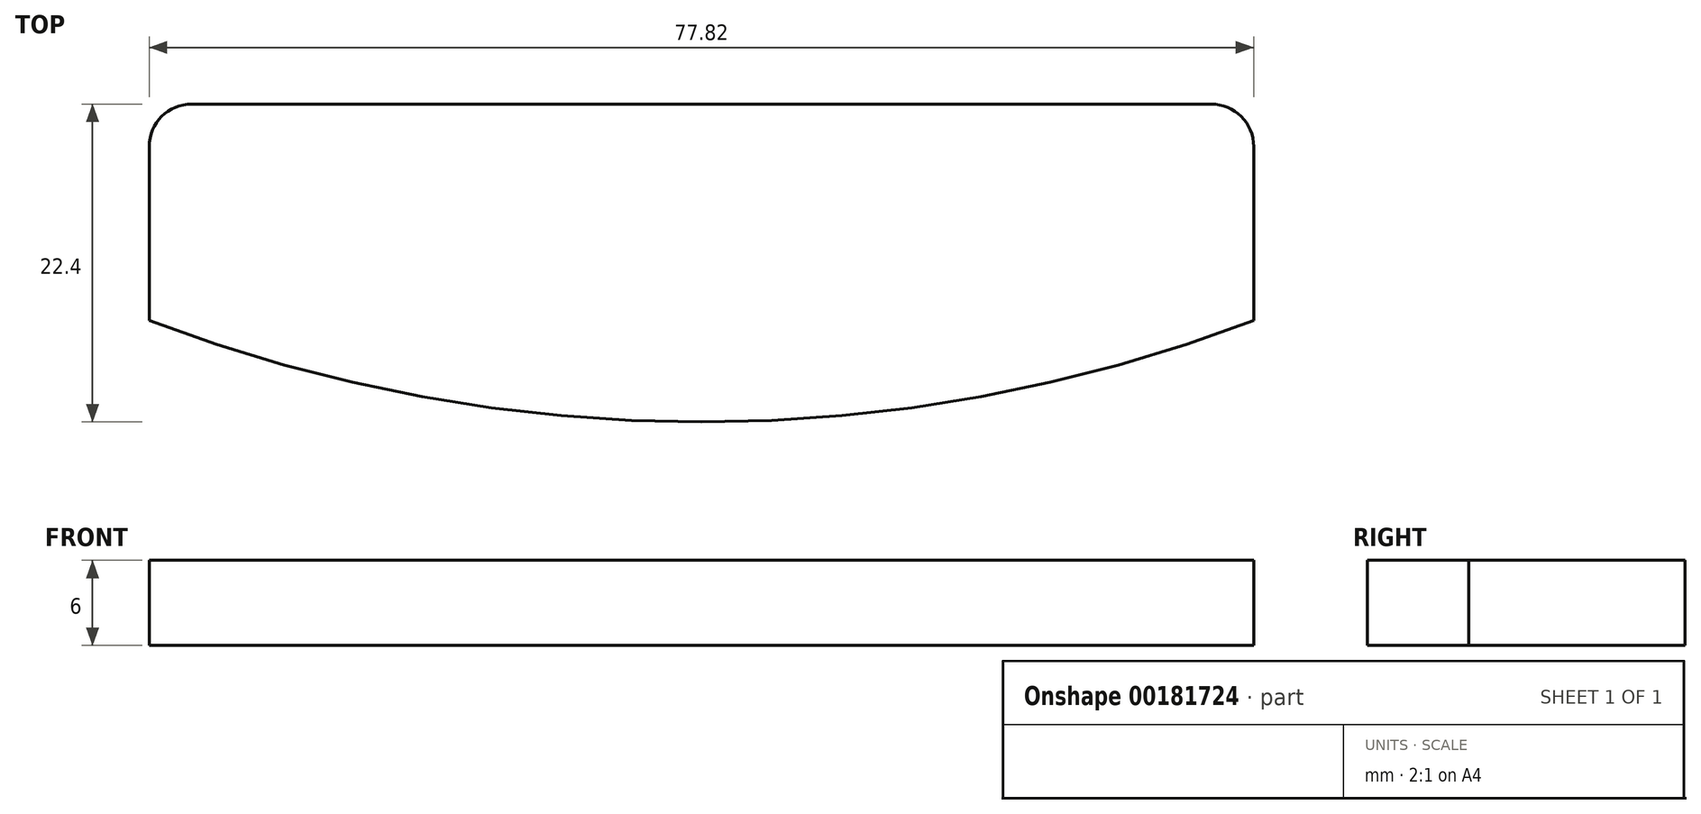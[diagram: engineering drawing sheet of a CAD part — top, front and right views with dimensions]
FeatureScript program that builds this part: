
annotation { "Feature Type Name" : "Feature", "Feature Type Description" : "" }
export const myFeature = defineFeature(function(context is Context, id is Id, definition is map)
    precondition{}
    {
        {
            var Q0;
            Q0=qCreatedBy(makeId("Top.planeOp"),FACE);
            var sketch = newSketch(context, id + "F0", { "sketchPlane" : qUnion([Q0])});
            skLineSegment(sketch, "E0.bottom", {"start": v(-35.07, 4.1) * mm, "end": v(36.75, 4.1) * mm});
            skLineSegment(sketch, "E0.top", {"start": v(-38.07, -11.15) * mm, "end": v(39.75, -11.15) * mm});
            skLineSegment(sketch, "E0.left", {"start": v(-38.07, 1.1) * mm, "end": v(-38.07, -11.15) * mm});
            skLineSegment(sketch, "E0.right", {"start": v(39.75, 1.1) * mm, "end": v(39.75, -11.15) * mm});
            skArc(sketch, "E1", {"start": v(-38.07, -11.15) * mm, "mid": v(0.84, -18.3) * mm, "end": v(39.75, -11.15) * mm});
            skPoint(sketch, "E2.visualSharp", {"position": v(-38.07, 4.1) * mm});
            skArc(sketch, "E2.filletArc", {"start": v(-35.07, 4.1) * mm, "mid": v(-37.19, 3.22) * mm, "end": v(-38.07, 1.1) * mm});
            skPoint(sketch, "E3.visualSharp", {"position": v(39.75, 4.1) * mm});
            skArc(sketch, "E3.filletArc", {"start": v(39.75, 1.1) * mm, "mid": v(38.87, 3.22) * mm, "end": v(36.75, 4.1) * mm});
            skSolve(sketch);
        }
        {
            var Q0;
            Q0=makeQuery(id+"F0.imprint","IMPRINT",FACE,{"disambiguationData":[TD([[makeQuery(id+"F0.imprint","IMPRINT",EDGE,{"derivedFrom":sQuery(id+"F0.wireOp",EDGE,"E0.bottom")}),-1.0]])]});
            var Q1;
            Q1=makeQuery(id+"F0.imprint","IMPRINT",FACE,{"disambiguationData":[TD([[makeQuery(id+"F0.imprint","IMPRINT",EDGE,{"derivedFrom":sQuery(id+"F0.wireOp",EDGE,"E0.top")}),-1.0]])]});
            extrude(context, id + "F1", {"entities" : qUnion([Q0, Q1]), "depth" : 6 * mm});
        }
    });
